# Revit family: Haworth_Masters_Drawer_Half
name_source: partatom
category: Furniture Systems
revit_build: Autodesk Revit 2018 (Build: 20170223_1515(x64)
units: mm (PartAtom-declared; Revit-internal decimal feet)

## family parameters
Always vertical = Yes
Cut with Voids When Loaded = No
Part Type = Normal
Room Calculation Point = No
Round Connector Dimension = Use Diameter
Shared = No
Work Plane-Based = No

## types (1)
- Haworth Drawer
    Assembly Code = E2020200
    Bar Pull Length = 30"
    Classic Pull Length = 6 3/4"
    Description = Haworth - Masters - Drawer - Half
    Drawer Finish = Haworth _ Wood _ White Oak
    Drawer Width = 36"
    Front Finish = Haworth _ Wood _ White Oak
    Manufacturer = Haworth
    Model = Haworth - Masters - Drawer - Half
    Pull Bar = No
    Pull Classic = No
    Pull Finish = Haworth _ Metal _ Brushed Aluminum
    Pull Height = 1 7/16"
    Pull Linear = No
    Revision Number = 2
    Sustainability Info = http://www.haworth.com
    URL = www.haworth.com
    URL - Product = http://www.haworth.com
    Warranty = http://www.haworth.com

## geometry (parser evidence)
native form markers: Sweep x5
no freeform markers — native parametric forms only
